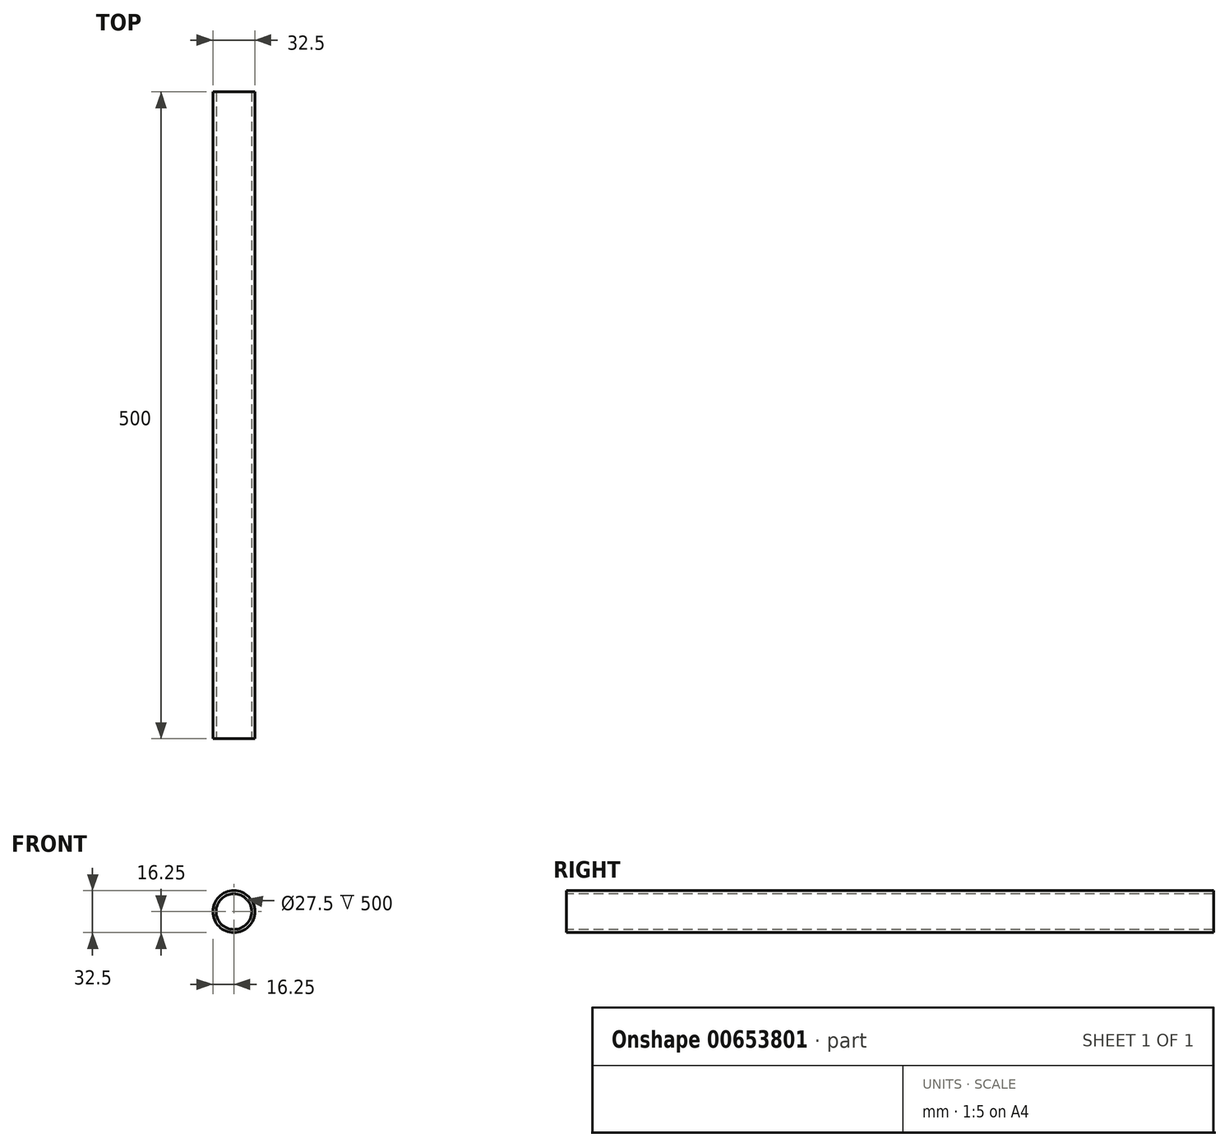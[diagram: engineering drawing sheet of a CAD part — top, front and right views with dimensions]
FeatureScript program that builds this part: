
annotation { "Feature Type Name" : "Feature", "Feature Type Description" : "" }
export const myFeature = defineFeature(function(context is Context, id is Id, definition is map)
    precondition{}
    {
        {
            var Q0;
            Q0=qCreatedBy(makeId("Front.planeOp"),FACE);
            var sketch = newSketch(context, id + "F0", { "sketchPlane" : qUnion([Q0])});
            skCircle(sketch, "E0", {"center": v(0, 0) * mm, "radius": 16.25 * mm});
            skSolve(sketch);
        }
        {
            var Q0;
            Q0 = qSketchRegion(id + "F0", true);
            extrude(context, id + "F1", {"entities" : qUnion([Q0]), "oppositeDirection" : true, "depth" : 500 * mm, "offsetDistance" : 25 * mm});
        }
        {
            var Q0;
            Q0=makeQuery(id+"F1.opExtrude","CAP_FACE",FACE,{"disambiguationData":[OSD([sQuery(id+"F0.wireOp",EDGE,"E0")])],"isStart":true});
            var Q1;
            Q1=makeQuery(id+"F1.opExtrude","CAP_FACE",FACE,{"disambiguationData":[OSD([sQuery(id+"F0.wireOp",EDGE,"E0")])],"isStart":false});
            shell(context, id + "F2", {"entities" : qUnion([Q0, Q1]), "thickness" : 2.5 * mm});
        }
    });
